# Revit family: AFX-Pearl_Vanity-
name_source: partatom
category: Lighting Fixtures
units: mm (PartAtom-declared; Revit-internal decimal feet)

## family parameters
Cut with Voids When Loaded = No
Host = Face
Light Source = Yes
Part Type = Normal
Room Calculation Point = No
Round Connector Dimension = Use Diameter
Shared = No

## types (2) — shared parameters
Apparent Load = 0 VA
Assembly Code = D5020200
Cap Finish = AFX - Black Steel
Color Filter = 16777215
Colour Rendering Index = 90
Cover Finish = AFX - Black Steel
Default Elevation = 48"
Depth = 5 1/2"
Diffuser Finish = AFX - White Acrylic
Dimming Lamp Color Temperature Shift = <None>
Frame Finish = AFX - Black Steel
Height = 7 1/2"
Housing Finish = AFX - Black Steel
Keynote = 12500
LED Finish = AFX - White Plastic
Manufacturer = AFX Inc
Product Documentation Link = https://www.afxinc.com
Revit File Built By = https://servex-us.com
Tilt Angle = 90.00°
Type Comments = Pearl
URL = https://www.afxinc.com
Voltage = 120 V

## per-type parameters (varying)
| type | Description | Length | Photometric Web File | Qty Lights | Wattage Comments |
| PRLV2408L30D1BK | Simplistic LED vanity available with three white glass globes - 24"L x 5 1/2"D x 7 1/2"H | 24" | PRLV2408L30D1GD.IES | 3 | 14 |
| PRLV3208L30D1BK | Simplistic LED vanity available with four white glass globes - 32"L x 5 1/2"D x 7 1/2"H | 32" | PRLV3208L30D1XX.IES | 4 | 21 |

note: column(s) folded — value = type name in every type: Model

## geometry (parser evidence)
native form markers: Sweep x3
no freeform markers — native parametric forms only
